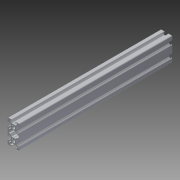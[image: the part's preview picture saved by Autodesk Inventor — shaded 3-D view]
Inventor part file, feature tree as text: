
AUTODESK INVENTOR PART (.ipt)
format: ipt  version: 2013 (Build 170138000, 138)  size: 480,768 bytes
history: native  units: in
note: dims shown in document units (in); Inventor stores cm internally (conversion verified against a paired STEP export)
features: other x3, extrude x1, sketch x1
ambient origin geometry x8: Origin, YZ Plane, XZ Plane, XY Plane, X Axis, Y Axis, Z Axis, Center Point
bodies: Solid1 (feature_tree)
feature tree (5):
  other  "Blocks"
  extrude  "Extrusion1"  [1 undecoded]
  sketch  "Sketch1"  dims[d1=0.0in]
  other  "Bosch 20x40 profile"
  other  "Bosch 20x40 profile:1"
note: 1 required parameter value undecoded (feature->parameter linkage not recoverable at this tier; creation-order binding heuristic only, values carry confidence <= 0.55)
